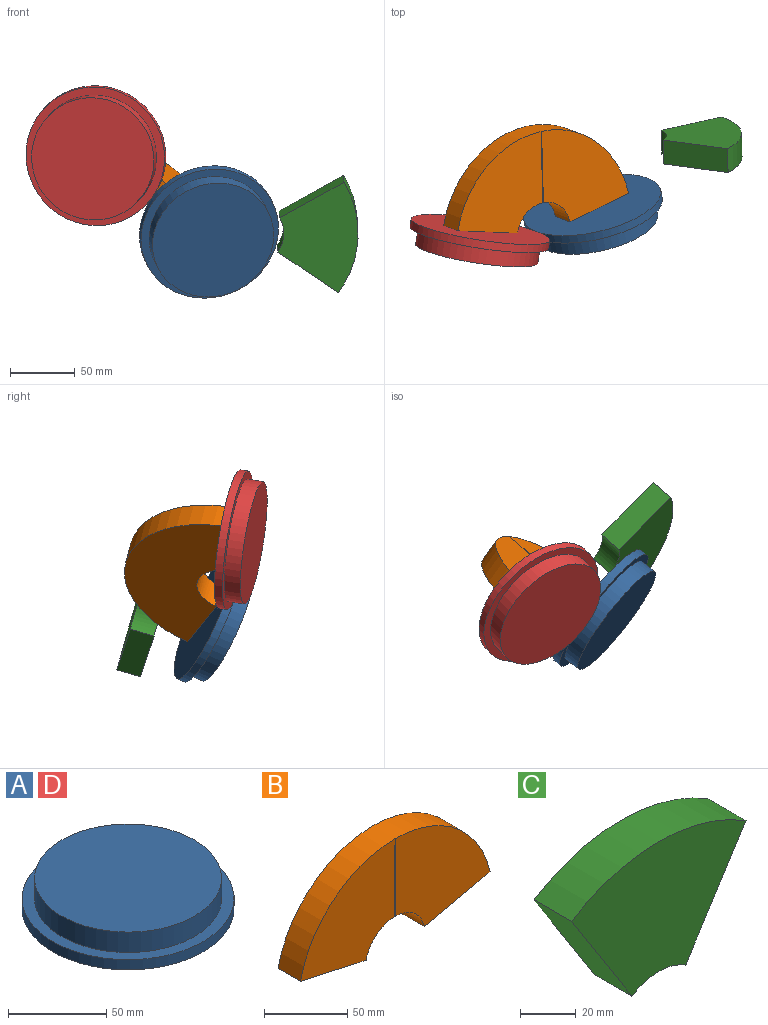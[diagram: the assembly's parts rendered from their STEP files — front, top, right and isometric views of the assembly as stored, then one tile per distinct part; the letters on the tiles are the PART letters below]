
ASSEMBLY  parts=4 mates=5
PART A: 5 faces, bbox 108x108x19.1 mm
  f0: cylinder r=53.98mm len=107.95mm, axis (0,0,-1), area 2153.5mm2, adj f1,f3
  f1: plane 107.95x107.95mm, normal (0,0,-1), area 9152.4mm2, adj f0
  f2: cylinder r=47.62mm len=95.25mm, axis (0,0,1), area 3800.3mm2, adj f3,f4
  f3: plane 107.95x107.95mm, normal (0,0,1), area 2026.8mm2, adj f0,f2
  f4: plane 95.25x95.25mm, normal (0,0,1), area 7125.6mm2, adj f2
PART B: 11 faces, bbox 161.2x19.1x77.1 mm
  f0: plane 80.36x77.07mm, normal (0,-1,0), area 4157.9mm2, adj f1,f2,f3,f9
  f1: cylinder r=25.4mm len=49.6mm, axis (0,1,0), area 1309mm2, adj f0,f2,f4,f5,f6,f8
  f2: plane 55.8x19.05mm, normal (0.22,0,-0.98), area 1088.7mm2, adj f0,f1,f3,f6
  f3: cylinder r=82.55mm len=161.19mm, axis (0,1,0), area 4254.2mm2, adj f0,f2,f4,f5,f6,f7,f9,f10
  f4: plane 55.8x19.05mm, normal (-0.22,0,-0.98), area 1088.7mm2, adj f1,f3,f5,f6
  f5: plane 80.36x77.07mm, normal (0,-1,0), area 4157.6mm2, adj f1,f3,f4,f7
  f6: plane 161.19x77.05mm, normal (0,1,0), area 8344.8mm2, adj f1,f2,f3,f4
  f7: plane 57.15x0.03mm, normal (-1,0,0), area 1.5mm2, adj f3,f5,f8,f10
  f8: plane 0.51x0.03mm, normal (0,0,-1), area 0mm2, adj f1,f7,f9,f10
  f9: plane 57.15x0.03mm, normal (1,0,0), area 1.5mm2, adj f0,f3,f8,f10
  f10: plane 57.15x0.51mm, normal (0,-1,0), area 29mm2, adj f3,f7,f8,f9
PART C: 6 faces, bbox 88.7x19.1x61.1 mm
  f0: cylinder r=25.4mm len=27.3mm, axis (0,1,0), area 548.9mm2, adj f1,f3,f4,f5
  f1: plane 48.2x30.71mm, normal (0.84,0,-0.54), area 1088.7mm2, adj f0,f2,f4,f5
  f2: cylinder r=82.55mm len=88.71mm, axis (0,1,0), area 1784mm2, adj f1,f3,f4,f5
  f3: plane 48.2x30.71mm, normal (-0.84,0,-0.54), area 1088.7mm2, adj f0,f2,f4,f5
  f4: plane 88.71x61.13mm, normal (0,-1,0), area 3499.4mm2, adj f0,f1,f2,f3
  f5: plane 88.71x61.13mm, normal (0,1,0), area 3499.4mm2, adj f0,f1,f2,f3
PART D: same geometry as A
PLACE A rot(axis=(0.21,0.83,-0.51),151.3deg) t=(77.71,61.5,-94.01)mm
PLACE B rot(axis=(-0.88,0.27,0.38),81.1deg) t=(29.51,42.84,-75.78)mm
PLACE C rot(axis=(0.12,0.98,0.15),93.7deg) t=(110.16,114.41,-91.37)mm
PLACE D rot(axis=(0.33,0.7,-0.64),158.8deg) t=(-8.23,42.52,-36.03)mm fixed
MATE planar B.f0 <-> C.f1  axis (0.58,-0.21,0.79) through (67.48,85.8,-67.79)mm
MATE cylindrical B.f4 <-> D.f0  axis (-0.15,-0.98,-0.15) through (-8.23,42.52,-36.03)mm
MATE cylindrical A.f0 <-> B.f2  axis (-0.2,0.9,0.39) through (77.71,61.5,-94.01)mm
MATE planar B.f2 <-> A.f0  axis (0.2,-0.9,-0.39) through (77.71,61.5,-94.01)mm
MATE planar B.f4 <-> D.f0  axis (-0.15,-0.98,-0.15) through (-8.23,42.52,-36.03)mm
